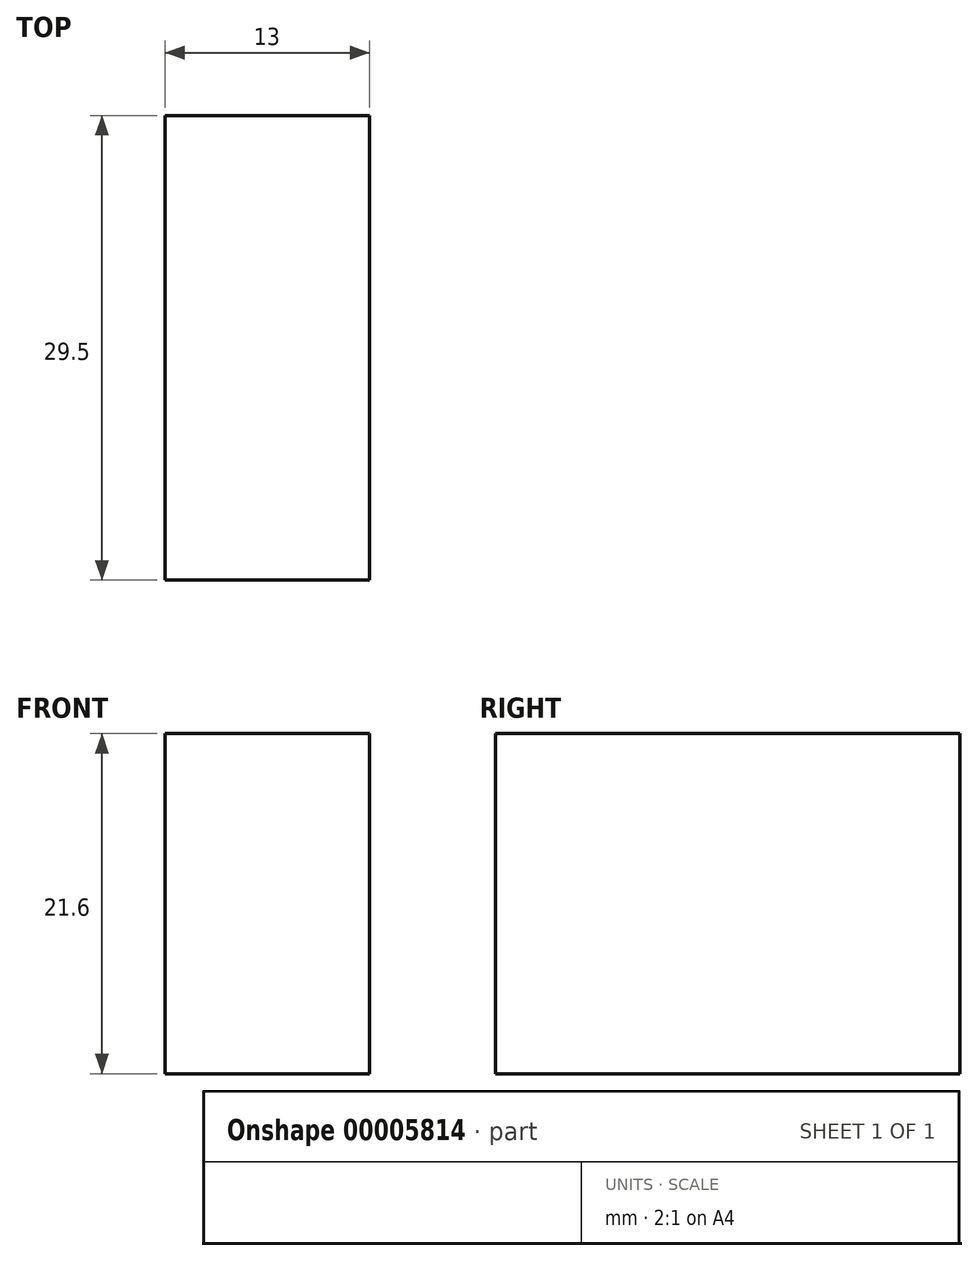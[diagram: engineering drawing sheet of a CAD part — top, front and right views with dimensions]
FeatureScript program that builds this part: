
annotation { "Feature Type Name" : "Feature", "Feature Type Description" : "" }
export const myFeature = defineFeature(function(context is Context, id is Id, definition is map)
    precondition{}
    {
        {
            var Q0;
            Q0=qCreatedBy(makeId("Top.planeOp"),FACE);
            var sketch = newSketch(context, id + "F0", { "sketchPlane" : qUnion([Q0])});
            skLineSegment(sketch, "E0.rect.bottom", {"start": v(6.5, -14.75) * mm, "end": v(-6.5, -14.75) * mm});
            skLineSegment(sketch, "E0.rect.top", {"start": v(6.5, 14.75) * mm, "end": v(-6.5, 14.75) * mm});
            skLineSegment(sketch, "E0.rect.left", {"start": v(6.5, -14.75) * mm, "end": v(6.5, 14.75) * mm});
            skLineSegment(sketch, "E0.rect.right", {"start": v(-6.5, -14.75) * mm, "end": v(-6.5, 14.75) * mm});
            skPoint(sketch, "E0.rect.middle", {"position": v(0, 0) * mm});
            skSolve(sketch);
        }
        {
            var Q0;
            Q0 = qSketchRegion(id + "F0", true);
            extrude(context, id + "F1", {"entities" : qUnion([Q0]), "depth" : 21.6 * mm});
        }
    });
